# Revit family: PN-照明分電箱-壁掛-共用-N-0
name_source: partatom
category: 電氣設備
revit_build: Autodesk Revit 2017 (Build: 20160225_1515(x64)
units: mm (PartAtom-declared; Revit-internal decimal feet)

## family parameters
OmniClass 標題 = Distribution Boards and Control Panels
OmniClass 編號 = 23.80.30.11.17
以工作平面為基礎 = 否
共用 = 是
圓形接點標註 = 使用直徑
房間計算點 = 否
組件類型 = 配電盤
總是垂直 = 是
載入時使用空心挖方 = 否
面板規劃 = 兩欄，回路穿越

## types (8) — shared parameters
品類 = 電氣設備
單位 = 組
單價 = 1
圖例說明 = 一般照明分電箱
工程用量 = 1
工項代碼 = M1647163338
工項名稱 = 照明分電箱-壁掛式 600(W)x200(D)x(800H)
把手W = 45  [stored 0.147638 ft]
設備名稱 = 一般照明分電箱
設備編號 = PN-100A
門鈑 = 15  [stored 0.0492126 ft]
預設高程 = 1800

## per-type parameters (varying)
| type | MCB 額定值 | 主幹線類型 | 把手H | 箱體D | 箱體H | 箱體W |
| 100A-600(W)x200(D)x(800H) | 15 A | 30 | 365  [stored 1.19751 ft] | 200  [stored 0.656168 ft] | 800  [stored 2.62467 ft] | 600 |
| 100A-650(W)x200(D)x(1200H) | 0 A |  | 565 | 200  [stored 0.656168 ft] | 1200 | 650 |
| 100A-480(W)x300(D)x(900H) | 0 A |  | 415 | 300 | 900 | 480 |
| 100A-480(W)x300(D)x(800H) | 0 A |  | 365  [stored 1.19751 ft] | 300 | 800  [stored 2.62467 ft] | 480 |
| 100A-750(W)x200(D)x(400H) | 0 A |  | 165 | 200  [stored 0.656168 ft] | 400  [stored 1.31234 ft] | 600 |
| 100A-400(W)x200(D)x(700H) | 0 A |  | 315 | 200  [stored 0.656168 ft] | 700 | 400  [stored 1.31234 ft] |
| 100A-600(W)x200(D)x(1200H) | 0 A |  | 565 | 200  [stored 0.656168 ft] | 1200 | 600 |
| 100A-600(W)x400(D)x(800H) | 0 A |  | 365  [stored 1.19751 ft] | 400  [stored 1.31234 ft] | 800  [stored 2.62467 ft] | 600 |

note: [stored X ft] marks values corroborated as IEEE doubles in the binary element streams (Revit-internal decimal feet)

## geometry (parser evidence)
native form markers: Blend x4
no freeform markers — native parametric forms only
